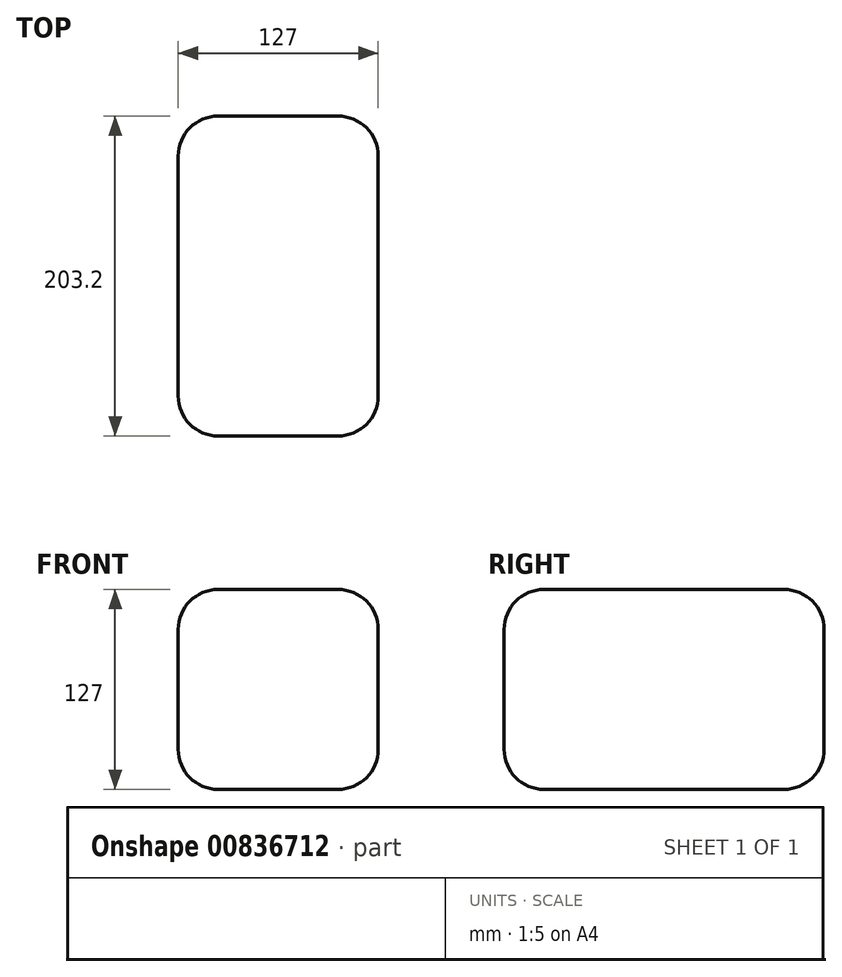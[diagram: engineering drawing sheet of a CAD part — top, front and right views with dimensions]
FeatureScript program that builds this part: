
annotation { "Feature Type Name" : "Feature", "Feature Type Description" : "" }
export const myFeature = defineFeature(function(context is Context, id is Id, definition is map)
    precondition{}
    {
        {
            var Q0;
            Q0=qCreatedBy(makeId("Front.planeOp"),FACE);
            var sketch = newSketch(context, id + "F0", { "sketchPlane" : qUnion([Q0])});
            skLineSegment(sketch, "E0.bottom", {"start": v(63.5, 63.5) * mm, "end": v(-63.5, 63.5) * mm});
            skLineSegment(sketch, "E0.top", {"start": v(63.5, -63.5) * mm, "end": v(-63.5, -63.5) * mm});
            skLineSegment(sketch, "E0.left", {"start": v(63.5, 63.5) * mm, "end": v(63.5, -63.5) * mm});
            skLineSegment(sketch, "E0.right", {"start": v(-63.5, 63.5) * mm, "end": v(-63.5, -63.5) * mm});
            skPoint(sketch, "E0.middle", {"position": v(0, 0) * mm});
            skSolve(sketch);
        }
        {
            var Q0;
            Q0 = qSketchRegion(id + "F0", true);
            extrude(context, id + "F1", {"entities" : qUnion([Q0]), "endBound" : BoundingType.SYMMETRIC, "depth" : 203.2 * mm, "offsetDistance" : 25.4 * mm});
        }
        {
            var Q0;
            Q0=makeQuery(id+"F1.opExtrude","SWEPT_EDGE",EDGE,{"disambiguationData":[OSD([sQuery(id+"F0.wireOp",EDGE,"E0.bottom"),sQuery(id+"F0.wireOp",EDGE,"E0.right")])]});
            var Q1;
            Q1=makeQuery(id+"F1.opExtrude","CAP_EDGE",EDGE,{"disambiguationData":[OSD([sQuery(id+"F0.wireOp",EDGE,"E0.bottom")])],"isStart":false});
            var Q2;
            Q2=makeQuery(id+"F1.opExtrude","SWEPT_EDGE",EDGE,{"disambiguationData":[OSD([sQuery(id+"F0.wireOp",EDGE,"E0.bottom"),sQuery(id+"F0.wireOp",EDGE,"E0.left")])]});
            var Q3;
            Q3=makeQuery(id+"F1.opExtrude","CAP_EDGE",EDGE,{"disambiguationData":[OSD([sQuery(id+"F0.wireOp",EDGE,"E0.bottom")])],"isStart":true});
            var Q4;
            Q4=makeQuery(id+"F1.opExtrude","CAP_EDGE",EDGE,{"disambiguationData":[OSD([sQuery(id+"F0.wireOp",EDGE,"E0.right")])],"isStart":false});
            var Q5;
            Q5=makeQuery(id+"F1.opExtrude","CAP_EDGE",EDGE,{"disambiguationData":[OSD([sQuery(id+"F0.wireOp",EDGE,"E0.left")])],"isStart":false});
            var Q6;
            Q6=makeQuery(id+"F1.opExtrude","CAP_EDGE",EDGE,{"disambiguationData":[OSD([sQuery(id+"F0.wireOp",EDGE,"E0.top")])],"isStart":false});
            var Q7;
            Q7=makeQuery(id+"F1.opExtrude","SWEPT_EDGE",EDGE,{"disambiguationData":[OSD([sQuery(id+"F0.wireOp",EDGE,"E0.top"),sQuery(id+"F0.wireOp",EDGE,"E0.right")])]});
            var Q8;
            Q8=makeQuery(id+"F1.opExtrude","CAP_EDGE",EDGE,{"disambiguationData":[OSD([sQuery(id+"F0.wireOp",EDGE,"E0.right")])],"isStart":true});
            var Q9;
            Q9=makeQuery(id+"F1.opExtrude","CAP_EDGE",EDGE,{"disambiguationData":[OSD([sQuery(id+"F0.wireOp",EDGE,"E0.left")])],"isStart":true});
            var Q10;
            Q10=makeQuery(id+"F1.opExtrude","SWEPT_EDGE",EDGE,{"disambiguationData":[OSD([sQuery(id+"F0.wireOp",EDGE,"E0.top"),sQuery(id+"F0.wireOp",EDGE,"E0.left")])]});
            var Q11;
            Q11=makeQuery(id+"F1.opExtrude","CAP_EDGE",EDGE,{"disambiguationData":[OSD([sQuery(id+"F0.wireOp",EDGE,"E0.top")])],"isStart":true});
            fillet(context, id + "F2", {"entities" : qUnion([Q0, Q1, Q2, Q3, Q4, Q5, Q6, Q7, Q8, Q9, Q10, Q11]), "radius" : 25.4 * mm, "tangentPropagation" : true, "allowEdgeOverflow" : false});
        }
    });
